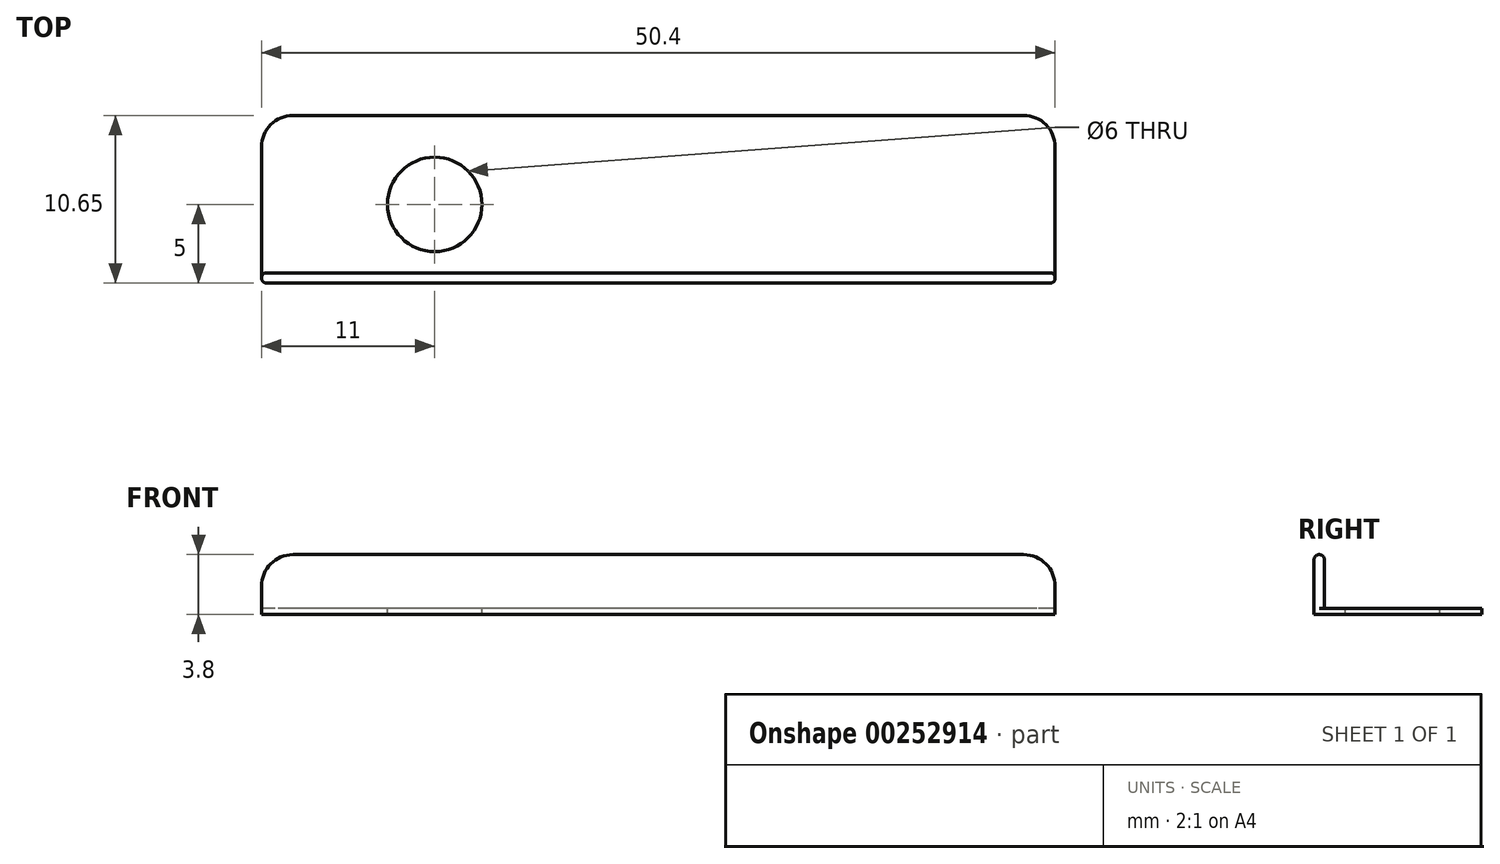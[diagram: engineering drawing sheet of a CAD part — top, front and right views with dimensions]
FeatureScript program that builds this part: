
annotation { "Feature Type Name" : "Feature", "Feature Type Description" : "" }
export const myFeature = defineFeature(function(context is Context, id is Id, definition is map)
    precondition{}
    {
        {
            var Q0;
            Q0=qCreatedBy(makeId("Right.planeOp"),FACE);
            var sketch = newSketch(context, id + "F0", { "sketchPlane" : qUnion([Q0])});
            skLineSegment(sketch, "E0", {"start": v(0, 0) * mm, "end": v(0, 3.8) * mm});
            skLineSegment(sketch, "E1", {"start": v(0, 3.8) * mm, "end": v(0.65, 3.8) * mm});
            skLineSegment(sketch, "E2", {"start": v(0.65, 3.8) * mm, "end": v(0.65, 0.4) * mm});
            skLineSegment(sketch, "E3", {"start": v(0.65, 0.4) * mm, "end": v(10.65, 0.4) * mm});
            skLineSegment(sketch, "E4", {"start": v(10.65, 0.4) * mm, "end": v(10.65, 0) * mm});
            skLineSegment(sketch, "E5", {"start": v(10.65, 0) * mm, "end": v(0, 0) * mm});
            skSolve(sketch);
        }
        {
            var Q0;
            Q0 = qSketchRegion(id + "F0", true);
            extrude(context, id + "F1", {"entities" : qUnion([Q0]), "depth" : 50.4 * mm});
        }
        {
            var Q0;
            Q0=makeQuery(id+"F1.opExtrude","SWEPT_FACE",FACE,{"disambiguationData":[OSD([sQuery(id+"F0.wireOp",EDGE,"E3")])]});
            var sketch = newSketch(context, id + "F2", { "sketchPlane" : qUnion([Q0])});
            skCircle(sketch, "E6", {"center": v(11, 5) * mm, "radius": 3 * mm});
            skSolve(sketch);
        }
        {
            var Q0;
            Q0 = qSketchRegion(id + "F2", true);
            extrude(context, id + "F3", {"entities" : qUnion([Q0]), "operationType" : NewBodyOperationType.REMOVE, "endBound" : BoundingType.THROUGH_ALL, "oppositeDirection" : true, "depth" : 25 * mm});
        }
        {
            var Q0;
            Q0=makeQuery(id+"F1.opExtrude","CAP_EDGE",EDGE,{"disambiguationData":[OSD([sQuery(id+"F0.wireOp",EDGE,"E4")])],"isStart":true});
            var Q1;
            Q1=makeQuery(id+"F1.opExtrude","CAP_EDGE",EDGE,{"disambiguationData":[OSD([sQuery(id+"F0.wireOp",EDGE,"E4")])],"isStart":false});
            var Q2;
            Q2=makeQuery(id+"F1.opExtrude","CAP_EDGE",EDGE,{"disambiguationData":[OSD([sQuery(id+"F0.wireOp",EDGE,"E1")])],"isStart":false});
            var Q3;
            Q3=makeQuery(id+"F1.opExtrude","CAP_EDGE",EDGE,{"disambiguationData":[OSD([sQuery(id+"F0.wireOp",EDGE,"E1")])],"isStart":true});
            fillet(context, id + "F4", {"entities" : qUnion([Q0, Q1, Q2, Q3]), "radius" : 2 * mm, "tangentPropagation" : true, "allowEdgeOverflow" : false});
        }
        {
            var Q0;
            Q0=makeQuery(id+"F1.opExtrude","CAP_EDGE",EDGE,{"disambiguationData":[OSD([sQuery(id+"F0.wireOp",EDGE,"E0")])],"isStart":true});
            var Q1;
            Q1=makeQuery(id+"F1.opExtrude","CAP_EDGE",EDGE,{"disambiguationData":[OSD([sQuery(id+"F0.wireOp",EDGE,"E0")])],"isStart":false});
            var Q2;
            Q2=makeQuery(id+"F1.opExtrude","CAP_EDGE",EDGE,{"disambiguationData":[OSD([sQuery(id+"F0.wireOp",EDGE,"E2")])],"isStart":false});
            var Q3;
            Q3=makeQuery(id+"F1.opExtrude","CAP_EDGE",EDGE,{"disambiguationData":[OSD([sQuery(id+"F0.wireOp",EDGE,"E2")])],"isStart":true});
            fillet(context, id + "F5", {"entities" : qUnion([Q0, Q1, Q2, Q3]), "radius" : 0.3 * mm, "tangentPropagation" : true, "allowEdgeOverflow" : false});
        }
    });
